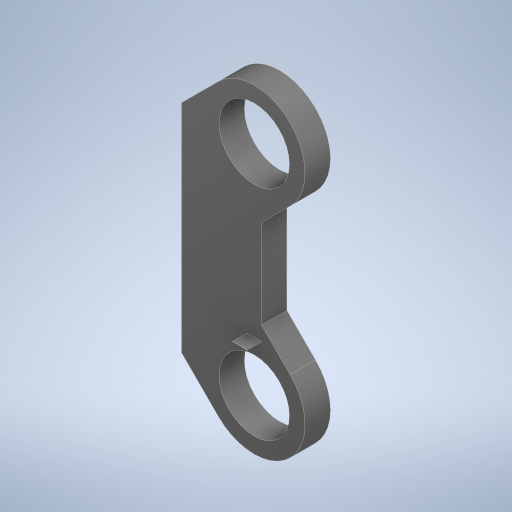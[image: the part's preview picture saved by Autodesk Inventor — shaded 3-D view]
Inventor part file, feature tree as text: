
AUTODESK INVENTOR PART (.ipt)
format: ipt  version: 2024.3 (Build 283343000, 343)  size: 273,920 bytes
history: native  units: in
note: dims shown in document units (in); Inventor stores cm internally (conversion verified against a paired STEP export)
features: extrude x1, sketch x1, other x1
ambient origin geometry x8: Origin, YZ Plane, XZ Plane, XY Plane, X Axis, Y Axis, Z Axis, Center Point
bodies: Solid1 (feature_tree)
feature tree (3):
  extrude  "Extrusion1"  [1 undecoded]
  sketch  "Sketch1"  dims[d0=0.0in d1=0.0in]
  other  "Saliente-Extruir3"
note: 1 required parameter value undecoded (feature->parameter linkage not recoverable at this tier; creation-order binding heuristic only, values carry confidence <= 0.55)
